# Revit family: Korpinen Handrail_
name_source: partatom
category: Casework
revit_build: Autodesk Revit Architecture 2012 (Build: 20110916_2132(x64)
units: mm (PartAtom-declared; Revit-internal decimal feet)

## types (8) — shared parameters
Height = 850 mm  [stored 2.78871 ft]
Manufacturer = Väinö Korpinen Oy
URL = www.korpinen.com

## per-type parameters (varying)
| type | Handrail Color | Length | Model |
| 1670 | Elastomer Coating Grey | 600 mm | 1670 Elastomere Coated Handrail |
| 1671 | Elastomer Coating Yellow | 600 mm | 1671 Elastomere Coated Handrail |
| 1673 | Elastomer Coating Red | 600 mm | 1673 Elastomere Coated Handrail |
| 1704 | Stainless Steel | 300 mm  [stored 0.984252 ft] | 1704 Stainless Steel Handrail |
| 1705 | Stainless Steel | 400 mm  [stored 1.31234 ft] | 1705 Stainless Steel Handrail |
| 1706 | Stainless Steel | 600 mm | 1706 Stainless Steel Handrail |
| 29082 | RAL 9016 - White | 300 mm  [stored 0.984252 ft] | 29082 Stainless Steel Handrail |
| 46391 | RAL 9016 - White | 600 mm | 46391 Stainless Steel Handrail |

note: [stored X ft] marks values corroborated as IEEE doubles in the binary element streams (Revit-internal decimal feet)

## geometry (parser evidence)
native form markers: Blend x2, Sweep x5
no freeform markers — native parametric forms only
